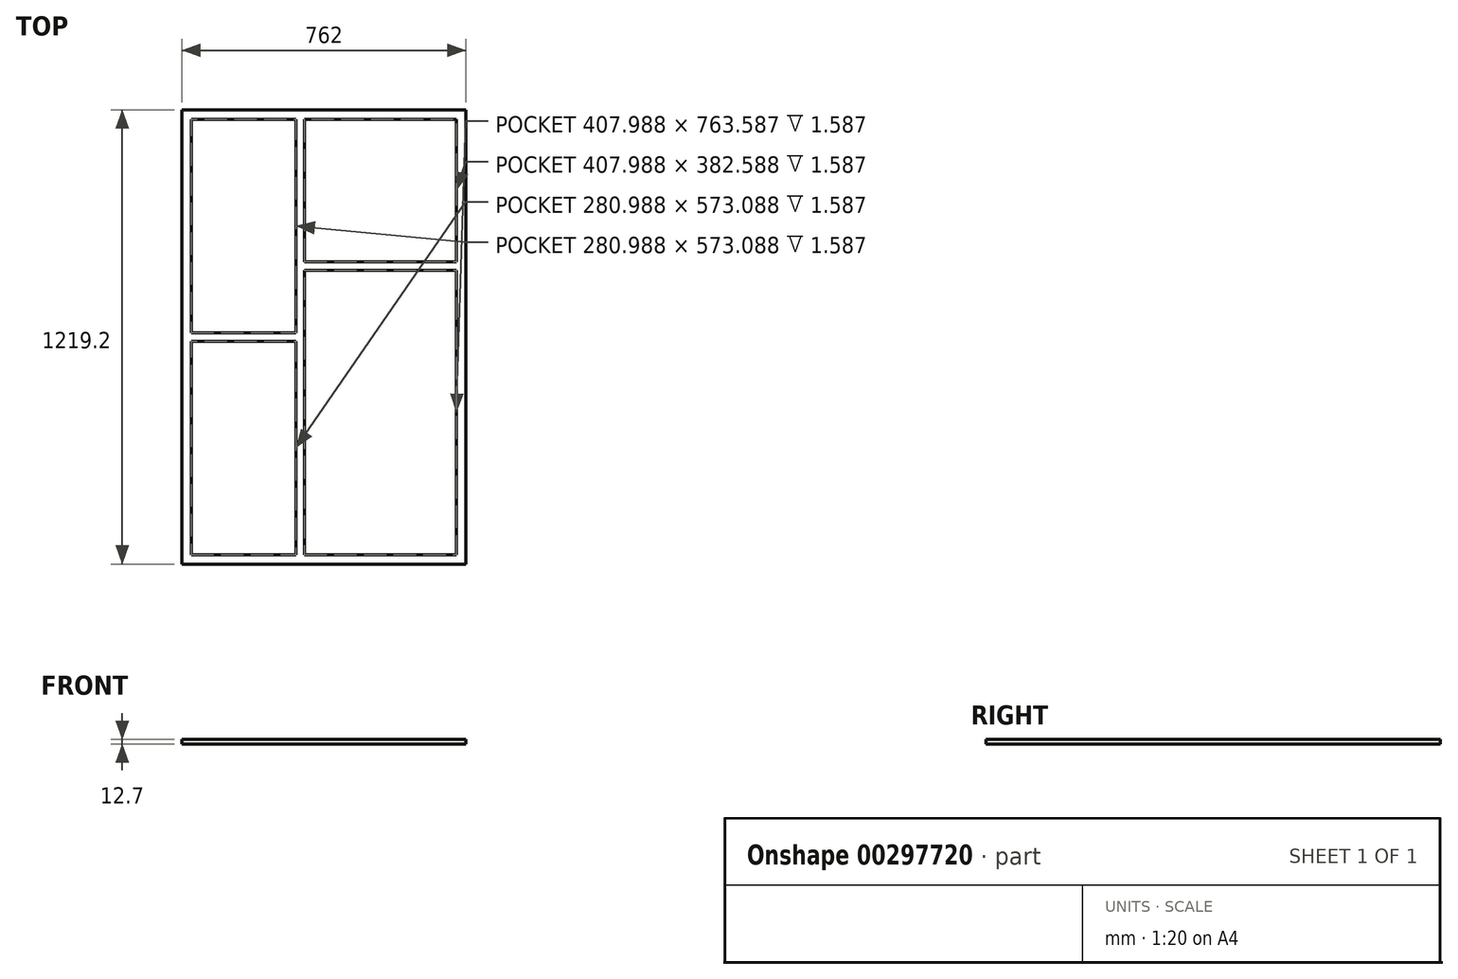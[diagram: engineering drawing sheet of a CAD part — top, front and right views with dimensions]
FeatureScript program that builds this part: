
annotation { "Feature Type Name" : "Feature", "Feature Type Description" : "" }
export const myFeature = defineFeature(function(context is Context, id is Id, definition is map)
    precondition{}
    {
        {
            var Q0;
            Q0=qCreatedBy(makeId("Top.planeOp"),FACE);
            var sketch = newSketch(context, id + "F0", { "sketchPlane" : qUnion([Q0])});
            skLineSegment(sketch, "E0.bottom", {"start": v(381, 609.6) * mm, "end": v(-381, 609.6) * mm});
            skLineSegment(sketch, "E0.top", {"start": v(381, -609.6) * mm, "end": v(-381, -609.6) * mm});
            skLineSegment(sketch, "E0.left", {"start": v(381, 609.6) * mm, "end": v(381, -609.6) * mm});
            skLineSegment(sketch, "E0.right", {"start": v(-381, 609.6) * mm, "end": v(-381, -609.6) * mm});
            skPoint(sketch, "E0.middle", {"position": v(0, 0) * mm});
            skSolve(sketch);
        }
        {
            var Q0;
            Q0 = qSketchRegion(id + "F0", true);
            extrude(context, id + "F1", {"entities" : qUnion([Q0]), "depth" : 12.7 * mm});
        }
        {
            var Q0;
            Q0=makeQuery(id+"F1.opExtrude","CAP_FACE",FACE,{"disambiguationData":[OSD([sQuery(id+"F0.wireOp",EDGE,"E0.bottom"),sQuery(id+"F0.wireOp",EDGE,"E0.top"),sQuery(id+"F0.wireOp",EDGE,"E0.left"),sQuery(id+"F0.wireOp",EDGE,"E0.right")])],"isStart":false});
            var sketch = newSketch(context, id + "F2", { "sketchPlane" : qUnion([Q0])});
            skLineSegment(sketch, "E1", {"start": v(381, -609.6) * mm, "end": v(355.61, -609.6) * mm, "construction": true});
            skLineSegment(sketch, "E2", {"start": v(355.61, -609.6) * mm, "end": v(355.61, -584.2) * mm, "construction": true});
            skLineSegment(sketch, "E3", {"start": v(355.61, -584.2) * mm, "end": v(381, -584.2) * mm, "construction": true});
            skLineSegment(sketch, "E4", {"start": v(381, -584.2) * mm, "end": v(381, -609.6) * mm, "construction": true});
            skSolve(sketch);
        }
        {
            var Q0;
            Q0=makeQuery(id+"F2.imprint","IMPRINT",FACE,{"disambiguationData":[TD([[makeQuery(id+"F2.imprint","IMPRINT",EDGE,{"derivedFrom":makeQuery(id+"F1.opExtrude","CAP_EDGE",EDGE,{"disambiguationData":[OSD([sQuery(id+"F0.wireOp",EDGE,"E0.bottom")])],"isStart":false})}),1.0]])]});
            var sketch = newSketch(context, id + "F3", { "sketchPlane" : qUnion([Q0])});
            skPoint(sketch, "E5.0", {"position": v(355.61, -584.2) * mm});
            skLineSegment(sketch, "E6", {"start": v(355.61, -584.2) * mm, "end": v(355.61, 179.4) * mm});
            skLineSegment(sketch, "E7", {"start": v(355.61, 179.4) * mm, "end": v(-52.38, 179.4) * mm});
            skLineSegment(sketch, "E8", {"start": v(-52.38, 179.4) * mm, "end": v(-52.38, -584.2) * mm});
            skLineSegment(sketch, "E9", {"start": v(-52.38, -584.2) * mm, "end": v(355.61, -584.2) * mm});
            skSolve(sketch);
        }
        {
            var Q0;
            Q0 = qSketchRegion(id + "F3", true);
            extrude(context, id + "F4", {"entities" : qUnion([Q0]), "operationType" : NewBodyOperationType.REMOVE, "oppositeDirection" : true, "depth" : 1.59 * mm});
        }
        {
            var Q0;
            Q0=makeQuery(id+"F2.imprint","IMPRINT",FACE,{"disambiguationData":[TD([[makeQuery(id+"F2.imprint","IMPRINT",EDGE,{"derivedFrom":makeQuery(id+"F1.opExtrude","CAP_EDGE",EDGE,{"disambiguationData":[OSD([sQuery(id+"F0.wireOp",EDGE,"E0.bottom")])],"isStart":false})}),1.0]])]});
            var sketch = newSketch(context, id + "F5", { "sketchPlane" : qUnion([Q0])});
            skPoint(sketch, "E10.0", {"position": v(381, 609.6) * mm});
            skLineSegment(sketch, "E11", {"start": v(381, 609.6) * mm, "end": v(355.6, 609.6) * mm, "construction": true});
            skLineSegment(sketch, "E12", {"start": v(355.6, 609.6) * mm, "end": v(355.6, 584.2) * mm, "construction": true});
            skLineSegment(sketch, "E13", {"start": v(355.6, 584.2) * mm, "end": v(381, 584.2) * mm, "construction": true});
            skLineSegment(sketch, "E14", {"start": v(381, 584.2) * mm, "end": v(381, 609.6) * mm, "construction": true});
            skSolve(sketch);
        }
        {
            var Q0;
            Q0=makeQuery(id+"F2.imprint","IMPRINT",FACE,{"disambiguationData":[TD([[makeQuery(id+"F2.imprint","IMPRINT",EDGE,{"derivedFrom":makeQuery(id+"F1.opExtrude","CAP_EDGE",EDGE,{"disambiguationData":[OSD([sQuery(id+"F0.wireOp",EDGE,"E0.bottom")])],"isStart":false})}),1.0]])]});
            var sketch = newSketch(context, id + "F6", { "sketchPlane" : qUnion([Q0])});
            skPoint(sketch, "E15.0", {"position": v(355.6, 584.2) * mm});
            skLineSegment(sketch, "E16", {"start": v(355.6, 584.2) * mm, "end": v(355.6, 201.61) * mm});
            skLineSegment(sketch, "E17", {"start": v(355.6, 201.61) * mm, "end": v(-52.39, 201.61) * mm});
            skLineSegment(sketch, "E18", {"start": v(-52.39, 201.61) * mm, "end": v(-52.39, 584.2) * mm});
            skLineSegment(sketch, "E19", {"start": v(-52.39, 584.2) * mm, "end": v(355.6, 584.2) * mm});
            skSolve(sketch);
        }
        {
            var Q0;
            Q0 = qSketchRegion(id + "F6", true);
            extrude(context, id + "F7", {"entities" : qUnion([Q0]), "operationType" : NewBodyOperationType.REMOVE, "oppositeDirection" : true, "depth" : 1.59 * mm});
        }
        {
            var Q0;
            Q0=makeQuery(id+"F2.imprint","IMPRINT",FACE,{"disambiguationData":[TD([[makeQuery(id+"F2.imprint","IMPRINT",EDGE,{"derivedFrom":makeQuery(id+"F1.opExtrude","CAP_EDGE",EDGE,{"disambiguationData":[OSD([sQuery(id+"F0.wireOp",EDGE,"E0.bottom")])],"isStart":false})}),1.0]])]});
            var sketch = newSketch(context, id + "F8", { "sketchPlane" : qUnion([Q0])});
            skPoint(sketch, "E20.0", {"position": v(-381, -609.6) * mm});
            skLineSegment(sketch, "E21", {"start": v(-381, -609.6) * mm, "end": v(-381, -584.2) * mm, "construction": true});
            skLineSegment(sketch, "E22", {"start": v(-381, -584.2) * mm, "end": v(-355.6, -584.2) * mm, "construction": true});
            skLineSegment(sketch, "E23", {"start": v(-355.6, -584.2) * mm, "end": v(-355.6, -609.6) * mm, "construction": true});
            skLineSegment(sketch, "E24", {"start": v(-355.6, -609.6) * mm, "end": v(-381, -609.6) * mm, "construction": true});
            skSolve(sketch);
        }
        {
            var Q0;
            Q0=makeQuery(id+"F2.imprint","IMPRINT",FACE,{"disambiguationData":[TD([[makeQuery(id+"F2.imprint","IMPRINT",EDGE,{"derivedFrom":makeQuery(id+"F1.opExtrude","CAP_EDGE",EDGE,{"disambiguationData":[OSD([sQuery(id+"F0.wireOp",EDGE,"E0.bottom")])],"isStart":false})}),1.0]])]});
            var sketch = newSketch(context, id + "F9", { "sketchPlane" : qUnion([Q0])});
            skPoint(sketch, "E25.0", {"position": v(-355.6, -584.2) * mm});
            skLineSegment(sketch, "E26", {"start": v(-355.6, -584.2) * mm, "end": v(-74.61, -584.2) * mm});
            skLineSegment(sketch, "E27", {"start": v(-74.61, -584.2) * mm, "end": v(-74.61, -11.11) * mm});
            skLineSegment(sketch, "E28", {"start": v(-74.61, -11.11) * mm, "end": v(-355.6, -11.11) * mm});
            skLineSegment(sketch, "E29", {"start": v(-355.6, -11.11) * mm, "end": v(-355.6, -584.2) * mm});
            skSolve(sketch);
        }
        {
            var Q0;
            Q0 = qSketchRegion(id + "F9", true);
            extrude(context, id + "F10", {"entities" : qUnion([Q0]), "operationType" : NewBodyOperationType.REMOVE, "oppositeDirection" : true, "depth" : 1.59 * mm});
        }
        {
            var Q0;
            Q0=makeQuery(id+"F2.imprint","IMPRINT",FACE,{"disambiguationData":[TD([[makeQuery(id+"F2.imprint","IMPRINT",EDGE,{"derivedFrom":makeQuery(id+"F1.opExtrude","CAP_EDGE",EDGE,{"disambiguationData":[OSD([sQuery(id+"F0.wireOp",EDGE,"E0.bottom")])],"isStart":false})}),1.0]])]});
            var sketch = newSketch(context, id + "F11", { "sketchPlane" : qUnion([Q0])});
            skPoint(sketch, "E30.0", {"position": v(-381, 609.6) * mm});
            skLineSegment(sketch, "E31", {"start": v(-381, 609.6) * mm, "end": v(-381, 584.2) * mm, "construction": true});
            skLineSegment(sketch, "E32", {"start": v(-381, 584.2) * mm, "end": v(-355.6, 584.2) * mm, "construction": true});
            skLineSegment(sketch, "E33", {"start": v(-355.6, 584.2) * mm, "end": v(-355.6, 609.6) * mm, "construction": true});
            skLineSegment(sketch, "E34", {"start": v(-355.6, 609.6) * mm, "end": v(-381, 609.6) * mm, "construction": true});
            skSolve(sketch);
        }
        {
            var Q0;
            Q0=makeQuery(id+"F2.imprint","IMPRINT",FACE,{"disambiguationData":[TD([[makeQuery(id+"F2.imprint","IMPRINT",EDGE,{"derivedFrom":makeQuery(id+"F1.opExtrude","CAP_EDGE",EDGE,{"disambiguationData":[OSD([sQuery(id+"F0.wireOp",EDGE,"E0.bottom")])],"isStart":false})}),1.0]])]});
            var sketch = newSketch(context, id + "F12", { "sketchPlane" : qUnion([Q0])});
            skPoint(sketch, "E35.0", {"position": v(-355.6, 584.2) * mm});
            skLineSegment(sketch, "E36", {"start": v(-355.6, 584.2) * mm, "end": v(-355.6, 11.11) * mm});
            skLineSegment(sketch, "E37", {"start": v(-355.6, 11.11) * mm, "end": v(-74.61, 11.11) * mm});
            skLineSegment(sketch, "E38", {"start": v(-74.61, 11.11) * mm, "end": v(-74.61, 584.2) * mm});
            skLineSegment(sketch, "E39", {"start": v(-74.61, 584.2) * mm, "end": v(-355.6, 584.2) * mm});
            skSolve(sketch);
        }
        {
            var Q0;
            Q0 = qSketchRegion(id + "F12", true);
            extrude(context, id + "F13", {"entities" : qUnion([Q0]), "operationType" : NewBodyOperationType.REMOVE, "oppositeDirection" : true, "depth" : 1.59 * mm});
        }
    });
